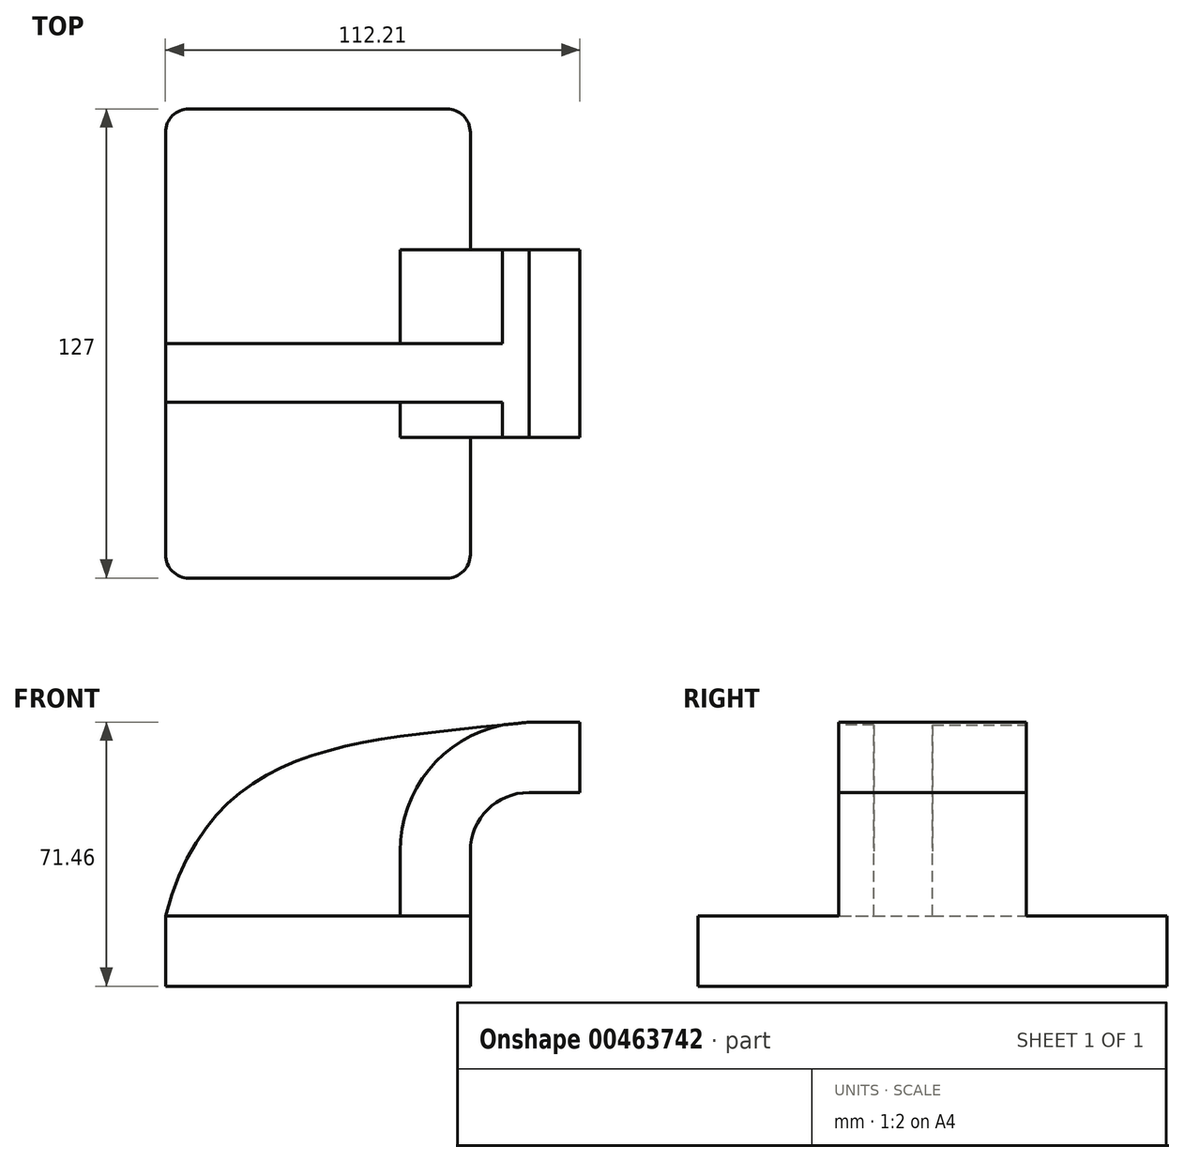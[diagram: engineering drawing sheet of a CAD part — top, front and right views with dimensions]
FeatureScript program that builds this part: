
annotation { "Feature Type Name" : "Feature", "Feature Type Description" : "" }
export const myFeature = defineFeature(function(context is Context, id is Id, definition is map)
    precondition{}
    {
        {
            var Q0;
            Q0=qCreatedBy(makeId("Front.planeOp"),FACE);
            var sketch = newSketch(context, id + "F0", { "sketchPlane" : qUnion([Q0])});
            skLineSegment(sketch, "E0.bottom", {"start": v(-41.28, 9.52) * mm, "end": v(41.27, 9.53) * mm});
            skLineSegment(sketch, "E0.top", {"start": v(-41.28, -9.53) * mm, "end": v(41.28, -9.53) * mm});
            skLineSegment(sketch, "E0.left", {"start": v(-41.28, 9.52) * mm, "end": v(-41.27, -9.53) * mm});
            skLineSegment(sketch, "E0.right", {"start": v(41.28, 9.53) * mm, "end": v(41.28, -9.52) * mm});
            skPoint(sketch, "E0.middle", {"position": v(0, 0) * mm});
            skLineSegment(sketch, "E1", {"start": v(41.27, 9.53) * mm, "end": v(41.27, 27) * mm});
            skArc(sketch, "E2", {"start": v(57.15, 42.88) * mm, "mid": v(45.92, 38.23) * mm, "end": v(41.27, 27) * mm});
            skLineSegment(sketch, "E3", {"start": v(57.15, 42.88) * mm, "end": v(70.93, 42.88) * mm});
            skLineSegment(sketch, "E4.bottom", {"start": v(111.13, 38.1) * mm, "end": v(60.32, 38.1) * mm});
            skLineSegment(sketch, "E4.top", {"start": v(111.13, 66.67) * mm, "end": v(60.33, 66.67) * mm});
            skLineSegment(sketch, "E4.left", {"start": v(111.13, 38.1) * mm, "end": v(111.13, 66.67) * mm});
            skLineSegment(sketch, "E4.right", {"start": v(60.32, 38.1) * mm, "end": v(60.33, 66.67) * mm});
            skPoint(sketch, "E4.middle", {"position": v(85.73, 52.39) * mm});
            skLineSegment(sketch, "E5.0", {"start": v(22.23, 9.53) * mm, "end": v(22.23, 27) * mm});
            skArc(sketch, "E5.1", {"start": v(57.15, 61.93) * mm, "mid": v(32.45, 51.7) * mm, "end": v(22.23, 27) * mm});
            skLineSegment(sketch, "E5.2", {"start": v(57.15, 61.93) * mm, "end": v(70.93, 61.93) * mm});
            skLineSegment(sketch, "E6", {"start": v(70.93, 61.93) * mm, "end": v(70.93, 42.88) * mm});
            skFitSpline(sketch, "E7", {"points": [v(-41.28, 9.53) * mm, v(57.15, 61.93) * mm], "startDerivative": vector(38.27, 141.9) * mm, "endDerivative": vector(145.26, 15.56) * mm});
            skSolve(sketch);
        }
        {
            var Q0;
            Q0=makeQuery(id+"F0.imprint","IMPRINT",FACE,{"disambiguationData":[TD([[makeQuery(id+"F0.imprint","IMPRINT",EDGE,{"derivedFrom":sQuery(id+"F0.wireOp",EDGE,"E0.top")}),1.0]])]});
            extrude(context, id + "F1", {"entities" : qUnion([Q0]), "depth" : 127 * mm, "symmetric" : true});
        }
        {
            var Q0;
            {var subQ9=sQuery(id+"F0.wireOp",EDGE,"E1");Q0=makeQuery(id+"F0.imprint","IMPRINT",FACE,{"disambiguationData":[TD([[makeQuery(id+"F0.imprint","IMPRINT",EDGE,{"derivedFrom":subQ9}),1.0]])]});}
            var Q1;
            {var subQ0=sQuery(id+"F0.wireOp",EDGE,"E6");Q1=makeQuery(id+"F0.imprint","IMPRINT",FACE,{"disambiguationData":[TD([[makeQuery(id+"F0.imprint","IMPRINT",EDGE,{"derivedFrom":subQ0}),-1.0]])]});}
            extrude(context, id + "F2", {"entities" : qUnion([Q0, Q1]), "operationType" : NewBodyOperationType.ADD, "depth" : 50.8 * mm, "symmetric" : true});
        }
        {
            var Q0;
            {var subQ3=sQuery(id+"F0.wireOp",EDGE,"E5.0");Q0=makeQuery(id+"F0.imprint","IMPRINT",FACE,{"disambiguationData":[TD([[makeQuery(id+"F0.imprint","IMPRINT",EDGE,{"derivedFrom":subQ3}),1.0]])]});}
            extrude(context, id + "F3", {"entities" : qUnion([Q0]), "operationType" : NewBodyOperationType.ADD, "depth" : 15.88 * mm});
        }
        {
            var Q0;
            Q0=makeQuery(id+"F1.opExtrude","CAP_EDGE",EDGE,{"disambiguationData":[OSD([sQuery(id+"F0.wireOp",EDGE,"E0.left")])],"isStart":false});
            var Q1;
            Q1=makeQuery(id+"F1.opExtrude","CAP_EDGE",EDGE,{"disambiguationData":[OSD([sQuery(id+"F0.wireOp",EDGE,"E0.right")])],"isStart":false});
            var Q2;
            Q2=makeQuery(id+"F1.opExtrude","CAP_EDGE",EDGE,{"disambiguationData":[OSD([sQuery(id+"F0.wireOp",EDGE,"E0.left")])],"isStart":true});
            var Q3;
            Q3=makeQuery(id+"F1.opExtrude","CAP_EDGE",EDGE,{"disambiguationData":[OSD([sQuery(id+"F0.wireOp",EDGE,"E0.right")])],"isStart":true});
            fillet(context, id + "F4", {"entities" : qUnion([Q0, Q1, Q2, Q3]), "radius" : 6.35 * mm, "tangentPropagation" : true, "allowEdgeOverflow" : false});
        }
    });
